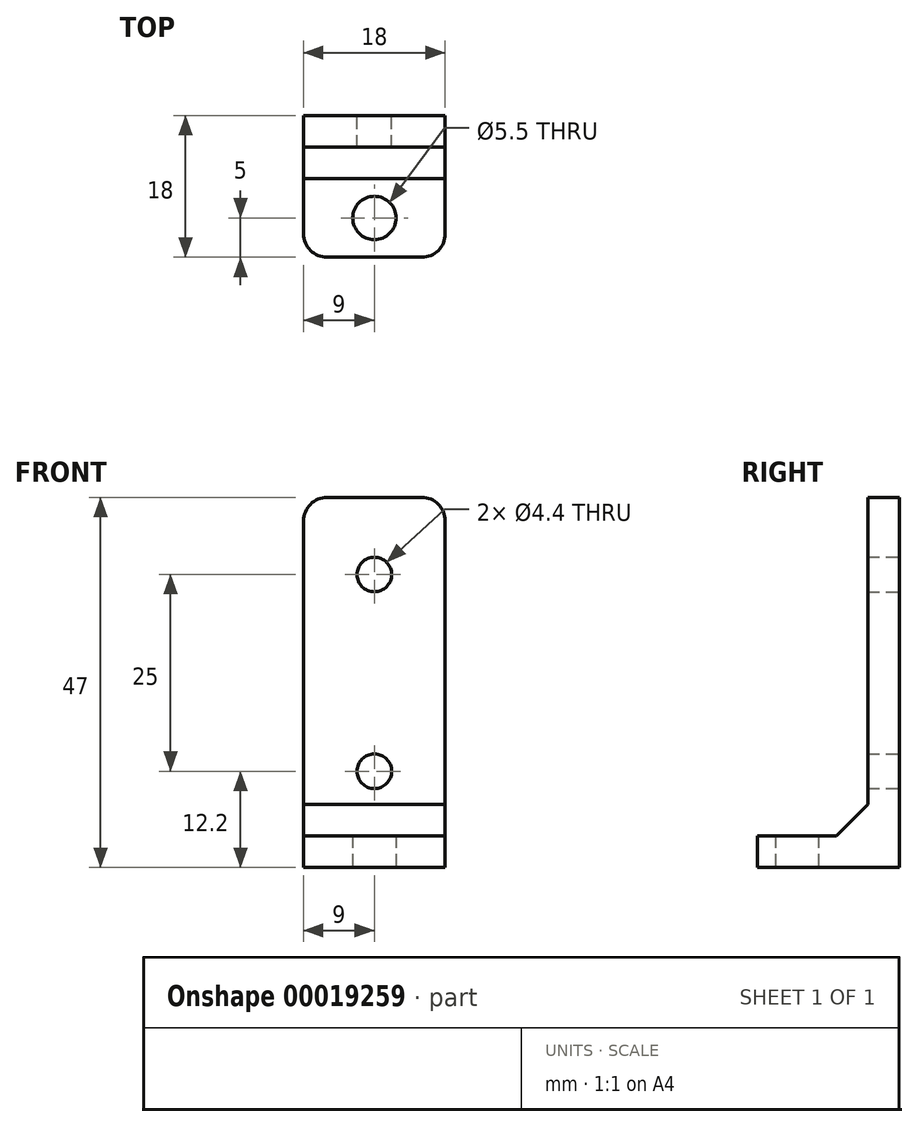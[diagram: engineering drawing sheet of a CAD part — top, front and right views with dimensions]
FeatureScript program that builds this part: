
annotation { "Feature Type Name" : "Feature", "Feature Type Description" : "" }
export const myFeature = defineFeature(function(context is Context, id is Id, definition is map)
    precondition{}
    {
        {
            var Q0;
            Q0=qCreatedBy(makeId("Front.planeOp"),FACE);
            var sketch = newSketch(context, id + "F0", { "sketchPlane" : qUnion([Q0])});
            skLineSegment(sketch, "E0.bottom", {"start": v(0, 0) * mm, "end": v(18, 0) * mm});
            skLineSegment(sketch, "E0.top", {"start": v(3, 47) * mm, "end": v(15, 47) * mm});
            skLineSegment(sketch, "E0.left", {"start": v(0, 0) * mm, "end": v(0, 44) * mm});
            skLineSegment(sketch, "E0.right", {"start": v(18, 0) * mm, "end": v(18, 44) * mm});
            skLineSegment(sketch, "E1", {"start": v(9, 47) * mm, "end": v(9, 0) * mm, "construction": true});
            skCircle(sketch, "E2", {"center": v(9, 12.2) * mm, "radius": 2.2 * mm});
            skCircle(sketch, "E3", {"center": v(9, 37.2) * mm, "radius": 2.2 * mm});
            skPoint(sketch, "E4.visualSharp", {"position": v(0, 47) * mm});
            skArc(sketch, "E4.filletArc", {"start": v(3, 47) * mm, "mid": v(0.88, 46.12) * mm, "end": v(0, 44) * mm});
            skPoint(sketch, "E5.visualSharp", {"position": v(18, 47) * mm});
            skArc(sketch, "E5.filletArc", {"start": v(18, 44) * mm, "mid": v(17.12, 46.12) * mm, "end": v(15, 47) * mm});
            skSolve(sketch);
        }
        {
            var Q0;
            Q0=qCreatedBy(makeId("Top.planeOp"),FACE);
            var sketch = newSketch(context, id + "F1", { "sketchPlane" : qUnion([Q0])});
            skLineSegment(sketch, "E6.bottom", {"start": v(0, 0) * mm, "end": v(18, 0) * mm});
            skLineSegment(sketch, "E6.top", {"start": v(3, -18) * mm, "end": v(15, -18) * mm});
            skLineSegment(sketch, "E6.left", {"start": v(0, 0) * mm, "end": v(0, -15) * mm});
            skLineSegment(sketch, "E6.right", {"start": v(18, 0) * mm, "end": v(18, -15) * mm});
            skCircle(sketch, "E7", {"center": v(9, -13) * mm, "radius": 2.75 * mm});
            skCircle(sketch, "E8", {"center": v(9, -13) * mm, "radius": 5 * mm});
            skPoint(sketch, "E9.visualSharp", {"position": v(0, -18) * mm});
            skArc(sketch, "E9.filletArc", {"start": v(0, -15) * mm, "mid": v(0.88, -17.12) * mm, "end": v(3, -18) * mm});
            skPoint(sketch, "E10.visualSharp", {"position": v(18, -18) * mm});
            skArc(sketch, "E10.filletArc", {"start": v(15, -18) * mm, "mid": v(17.12, -17.12) * mm, "end": v(18, -15) * mm});
            skLineSegment(sketch, "E11", {"start": v(9, 0) * mm, "end": v(9, -18) * mm, "construction": true});
            skSolve(sketch);
        }
        {
            var Q0;
            Q0=makeQuery(id+"F1.imprint","IMPRINT",FACE,{"disambiguationData":[TD([[makeQuery(id+"F1.imprint","IMPRINT",EDGE,{"derivedFrom":sQuery(id+"F1.wireOp",EDGE,"E6.bottom")}),-1.0]])]});
            var Q1;
            Q1=makeQuery(id+"F1.imprint","IMPRINT",FACE,{"disambiguationData":[TD([[makeQuery(id+"F1.imprint","IMPRINT",EDGE,{"derivedFrom":sQuery(id+"F1.wireOp",EDGE,"E7")}),-1.0]])]});
            extrude(context, id + "F2", {"entities" : qUnion([Q0, Q1]), "depth" : 4 * mm});
        }
        {
            var Q0;
            Q0=makeQuery(id+"F0.imprint","IMPRINT",FACE,{"disambiguationData":[TD([[makeQuery(id+"F0.imprint","IMPRINT",EDGE,{"derivedFrom":sQuery(id+"F0.wireOp",EDGE,"E0.bottom")}),1.0]])]});
            extrude(context, id + "F3", {"entities" : qUnion([Q0]), "operationType" : NewBodyOperationType.ADD, "depth" : 4 * mm});
        }
        {
            var Q0;
            Q0=makeQuery(id+"F3.boolean.opBoolean","INTERSECT",EDGE,{"derivedFrom":[makeQuery(id+"F2.opExtrude","CAP_FACE",FACE,{"disambiguationData":[OSD([sQuery(id+"F1.wireOp",EDGE,"E6.bottom"),sQuery(id+"F1.wireOp",EDGE,"E6.top"),sQuery(id+"F1.wireOp",EDGE,"E6.left"),sQuery(id+"F1.wireOp",EDGE,"E6.right"),sQuery(id+"F1.wireOp",EDGE,"E7"),sQuery(id+"F1.wireOp",EDGE,"E9.filletArc"),sQuery(id+"F1.wireOp",EDGE,"E10.filletArc")])],"isStart":false}),makeQuery(id+"F3.opExtrude","CAP_FACE",FACE,{"disambiguationData":[OSD([sQuery(id+"F0.wireOp",EDGE,"E0.bottom"),sQuery(id+"F0.wireOp",EDGE,"E0.top"),sQuery(id+"F0.wireOp",EDGE,"E0.left"),sQuery(id+"F0.wireOp",EDGE,"E0.right"),sQuery(id+"F0.wireOp",EDGE,"E2"),sQuery(id+"F0.wireOp",EDGE,"E3"),sQuery(id+"F0.wireOp",EDGE,"E4.filletArc"),sQuery(id+"F0.wireOp",EDGE,"E5.filletArc")])],"isStart":false})]});
            chamfer(context, id + "F4", {"entities" : qUnion([Q0]), "width" : 4 * mm, "tangentPropagation" : true});
        }
    });
